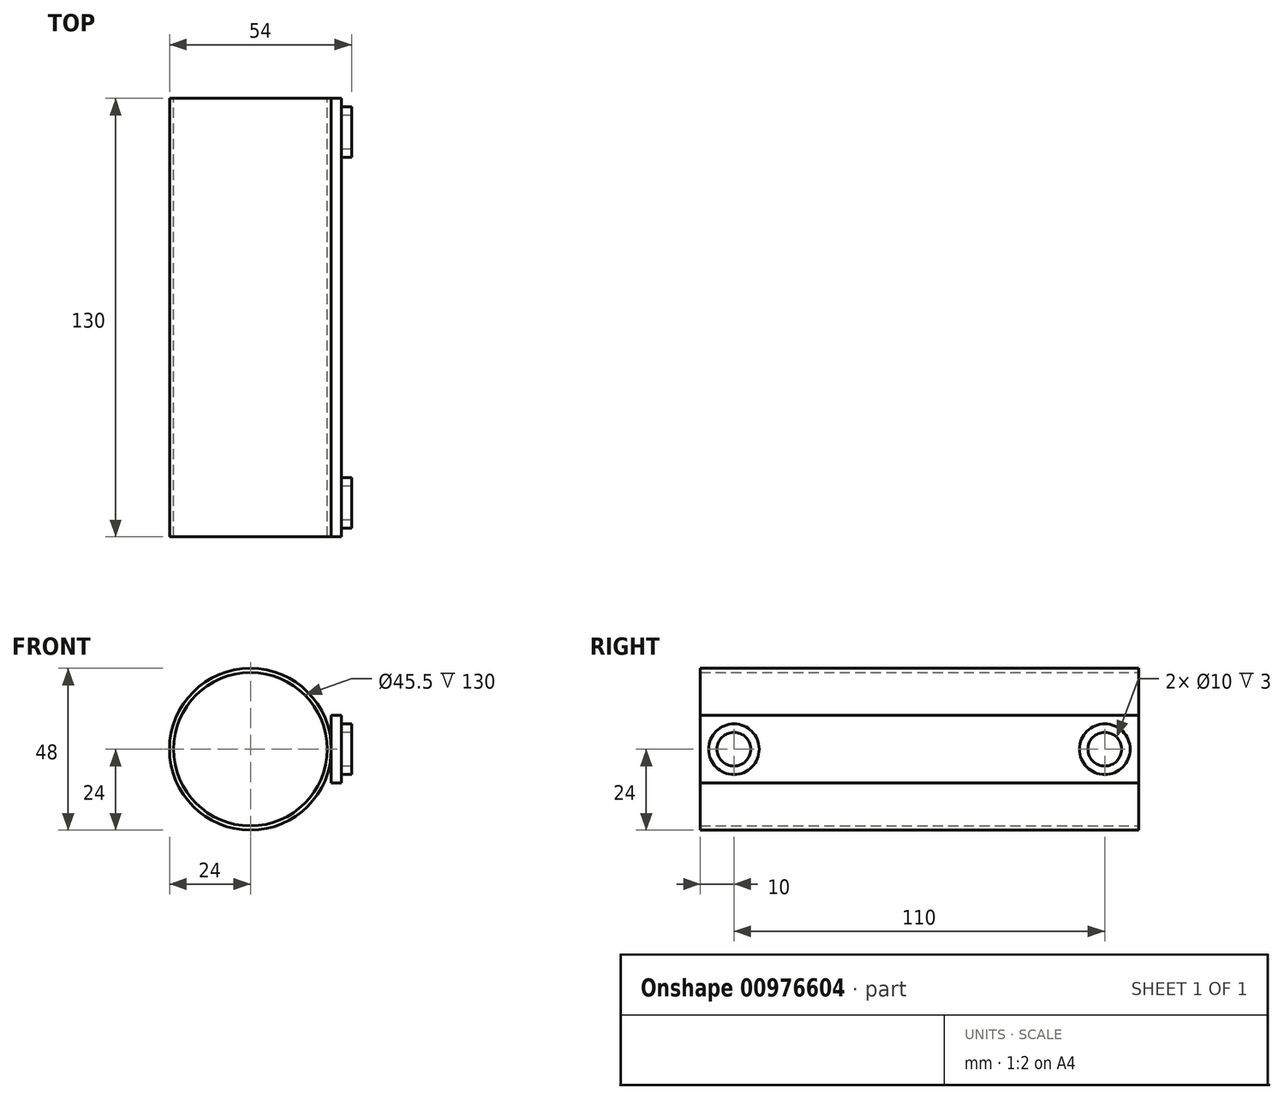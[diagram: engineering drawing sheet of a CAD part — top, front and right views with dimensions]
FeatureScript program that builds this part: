
annotation { "Feature Type Name" : "Feature", "Feature Type Description" : "" }
export const myFeature = defineFeature(function(context is Context, id is Id, definition is map)
    precondition{}
    {
        {
            var Q0;
            Q0=qCreatedBy(makeId("Front.planeOp"),FACE);
            var sketch = newSketch(context, id + "F0", { "sketchPlane" : qUnion([Q0])});
            skCircle(sketch, "E0", {"center": v(0, 0) * mm, "radius": 24 * mm});
            skCircle(sketch, "E1", {"center": v(0, 0) * mm, "radius": 22.75 * mm});
            skSolve(sketch);
        }
        {
            var Q0;
            Q0=makeQuery(id+"F0.imprint","IMPRINT",FACE,{"disambiguationData":[TD([[makeQuery(id+"F0.imprint","IMPRINT",EDGE,{"derivedFrom":sQuery(id+"F0.wireOp",EDGE,"E0")}),1.0]])]});
            extrude(context, id + "F1", {"entities" : qUnion([Q0]), "depth" : 130 * mm, "offsetDistance" : 25 * mm, "symmetric" : true});
        }
        {
            var Q0;
            Q0=makeQuery(id+"F1.opExtrude","CAP_FACE",FACE,{"disambiguationData":[OSD([sQuery(id+"F0.wireOp",EDGE,"E0"),sQuery(id+"F0.wireOp",EDGE,"E1")])],"isStart":false});
            var sketch = newSketch(context, id + "F2", { "sketchPlane" : qUnion([Q0])});
            skLineSegment(sketch, "E2", {"start": v(24, 0) * mm, "end": v(24, 10) * mm});
            skLineSegment(sketch, "E3", {"start": v(24, 0) * mm, "end": v(24, -10) * mm});
            skLineSegment(sketch, "E4.bottom", {"start": v(24, 10) * mm, "end": v(27, 10) * mm});
            skLineSegment(sketch, "E4.top", {"start": v(24, -10) * mm, "end": v(27, -10) * mm});
            skLineSegment(sketch, "E4.left", {"start": v(24, 10) * mm, "end": v(24, -10) * mm});
            skLineSegment(sketch, "E4.right", {"start": v(27, 10) * mm, "end": v(27, -10) * mm});
            skSolve(sketch);
        }
        {
            var Q0;
            Q0=makeQuery(id+"F2.imprint","IMPRINT",FACE,{"disambiguationData":[TD([[makeQuery(id+"F2.imprint","IMPRINT",EDGE,{"derivedFrom":sQuery(id+"F2.wireOp",EDGE,"E2")}),-1.0]])]});
            extrude(context, id + "F3", {"entities" : qUnion([Q0]), "oppositeDirection" : true, "depth" : 130 * mm, "offsetDistance" : 25 * mm});
        }
        {
            var Q0;
            Q0=makeQuery(id+"F3.opExtrude","SWEPT_FACE",FACE,{"disambiguationData":[OSD([sQuery(id+"F2.wireOp",EDGE,"E4.right")])]});
            var sketch = newSketch(context, id + "F4", { "sketchPlane" : qUnion([Q0])});
            skLineSegment(sketch, "E5", {"start": v(0, 0) * mm, "end": v(-55, 0) * mm});
            skLineSegment(sketch, "E6", {"start": v(0, 0) * mm, "end": v(55, 0) * mm});
            skCircle(sketch, "E7", {"center": v(55, 0) * mm, "radius": 7.5 * mm});
            skCircle(sketch, "E8", {"center": v(55, 0) * mm, "radius": 5 * mm});
            skCircle(sketch, "E9", {"center": v(-55, 0) * mm, "radius": 7.5 * mm});
            skCircle(sketch, "E10", {"center": v(-55, 0) * mm, "radius": 5 * mm});
            skSolve(sketch);
        }
        {
            var Q0;
            Q0 = qSketchRegion(id + "F4", true);
            extrude(context, id + "F5", {"entities" : qUnion([Q0]), "depth" : 3 * mm, "offsetDistance" : 25 * mm});
        }
    });
